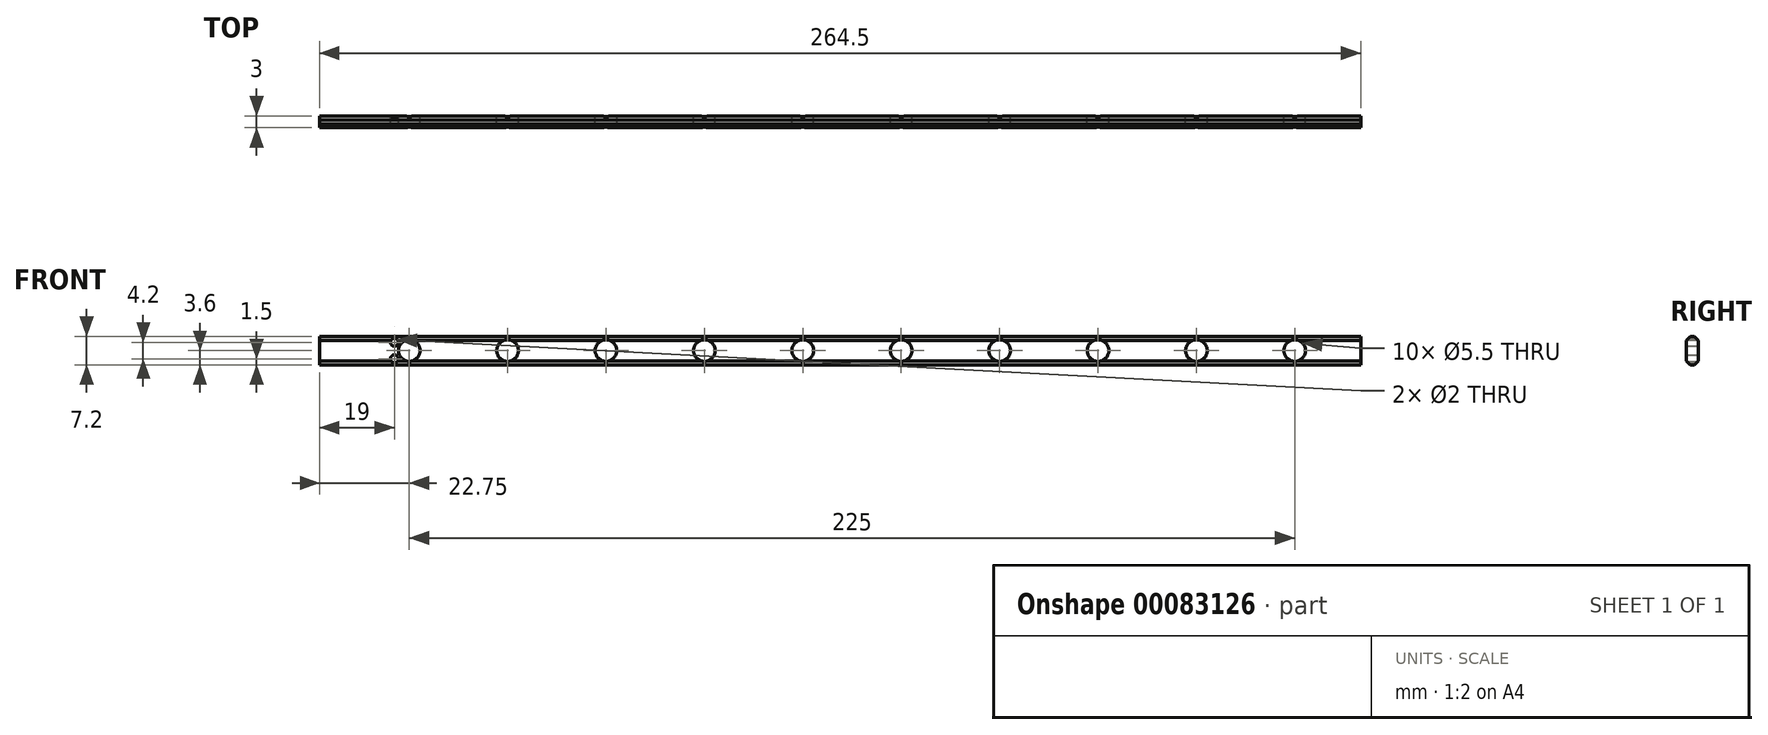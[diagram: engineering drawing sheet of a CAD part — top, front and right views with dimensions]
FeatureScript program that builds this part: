
annotation { "Feature Type Name" : "Feature", "Feature Type Description" : "" }
export const myFeature = defineFeature(function(context is Context, id is Id, definition is map)
    precondition{}
    {
        {
            var Q0;
            Q0=qCreatedBy(makeId("Front.planeOp"),FACE);
            var sketch = newSketch(context, id + "F0", { "sketchPlane" : qUnion([Q0])});
            skLineSegment(sketch, "E0.bottom", {"start": v(-132.25, 3.6) * mm, "end": v(132.25, 3.6) * mm});
            skLineSegment(sketch, "E0.top", {"start": v(-132.25, -3.6) * mm, "end": v(132.25, -3.6) * mm});
            skLineSegment(sketch, "E0.left", {"start": v(-132.25, 3.6) * mm, "end": v(-132.25, -3.6) * mm});
            skLineSegment(sketch, "E0.right", {"start": v(132.25, 3.6) * mm, "end": v(132.25, -3.6) * mm});
            skPoint(sketch, "E0.middle", {"position": v(0, 0) * mm});
            skCircle(sketch, "E1", {"center": v(-109.5, 0) * mm, "radius": 2.75 * mm});
            skCircle(sketch, "E2.1.0.0", {"center": v(-84.5, 0) * mm, "radius": 2.75 * mm});
            skCircle(sketch, "E2.2.0.0", {"center": v(-59.5, 0) * mm, "radius": 2.75 * mm});
            skCircle(sketch, "E2.3.0.0", {"center": v(-34.5, 0) * mm, "radius": 2.75 * mm});
            skCircle(sketch, "E2.4.0.0", {"center": v(-9.5, 0) * mm, "radius": 2.75 * mm});
            skCircle(sketch, "E2.5.0.0", {"center": v(15.5, 0) * mm, "radius": 2.75 * mm});
            skCircle(sketch, "E2.6.0.0", {"center": v(40.5, 0) * mm, "radius": 2.75 * mm});
            skCircle(sketch, "E2.7.0.0", {"center": v(65.5, 0) * mm, "radius": 2.75 * mm});
            skCircle(sketch, "E2.8.0.0", {"center": v(90.5, 0) * mm, "radius": 2.75 * mm});
            skCircle(sketch, "E2.9.0.0", {"center": v(115.5, 0) * mm, "radius": 2.75 * mm});
            skLineSegment(sketch, "E2.direction1", {"start": v(-109.5, 0) * mm, "end": v(-84.5, 0) * mm, "construction": true});
            skCircle(sketch, "E3", {"center": v(-113.25, 2.1) * mm, "radius": 1 * mm});
            skCircle(sketch, "E4.MirrorC", {"center": v(-113.25, -2.1) * mm, "radius": 1 * mm});
            skSolve(sketch);
        }
        {
            var Q0;
            Q0=makeQuery(id+"F0.imprint","IMPRINT",FACE,{"disambiguationData":[TD([[makeQuery(id+"F0.imprint","IMPRINT",EDGE,{"derivedFrom":sQuery(id+"F0.wireOp",EDGE,"E0.bottom")}),-1.0]])]});
            extrude(context, id + "F1", {"entities" : qUnion([Q0]), "depth" : 3 * mm});
        }
        {
            var Q0;
            Q0=makeQuery(id+"F1.opExtrude","CAP_EDGE",EDGE,{"disambiguationData":[OSD([sQuery(id+"F0.wireOp",EDGE,"E0.top")])],"isStart":false});
            var Q1;
            Q1=makeQuery(id+"F1.opExtrude","CAP_EDGE",EDGE,{"disambiguationData":[OSD([sQuery(id+"F0.wireOp",EDGE,"E0.top")])],"isStart":true});
            var Q2;
            Q2=makeQuery(id+"F1.opExtrude","CAP_EDGE",EDGE,{"disambiguationData":[OSD([sQuery(id+"F0.wireOp",EDGE,"E0.bottom")])],"isStart":true});
            var Q3;
            Q3=makeQuery(id+"F1.opExtrude","CAP_EDGE",EDGE,{"disambiguationData":[OSD([sQuery(id+"F0.wireOp",EDGE,"E0.bottom")])],"isStart":false});
            chamfer(context, id + "F2", {"entities" : qUnion([Q0, Q1, Q2, Q3]), "width" : 1 * mm, "tangentPropagation" : true});
        }
    });
